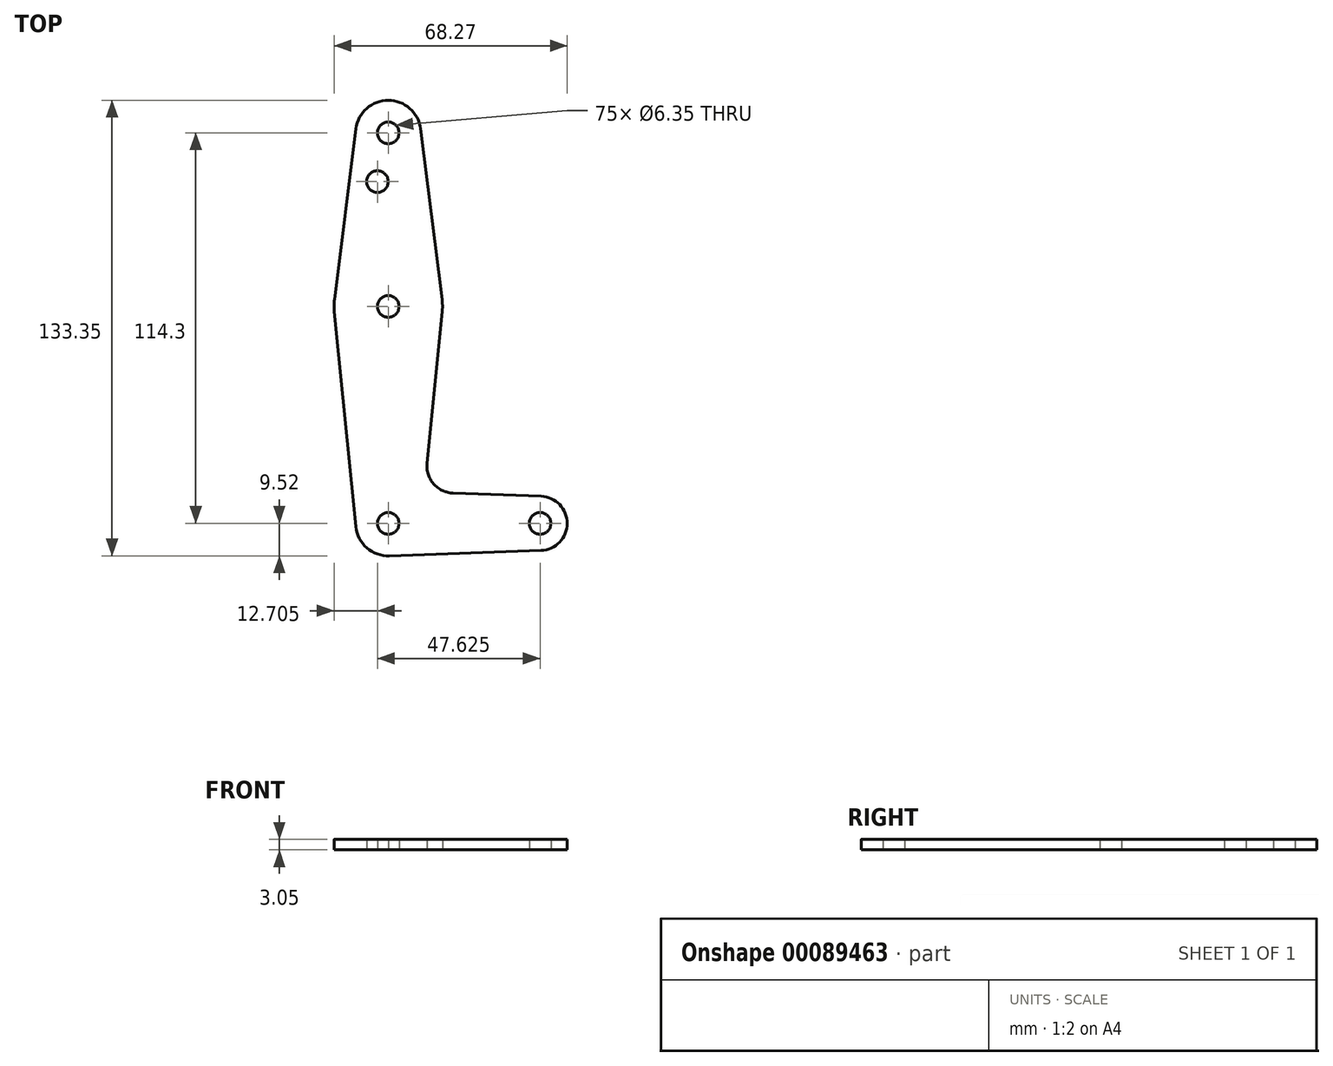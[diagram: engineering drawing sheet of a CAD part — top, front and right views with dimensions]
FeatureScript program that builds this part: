
annotation { "Feature Type Name" : "Feature", "Feature Type Description" : "" }
export const myFeature = defineFeature(function(context is Context, id is Id, definition is map)
    precondition{}
    {
        {
            var Q0;
            Q0=qCreatedBy(makeId("Top.planeOp"),FACE);
            var sketch = newSketch(context, id + "F0", { "sketchPlane" : qUnion([Q0])});
            skLineSegment(sketch, "E0", {"start": v(0, 0) * mm, "end": v(0, 114.3) * mm, "construction": true});
            skLineSegment(sketch, "E1", {"start": v(0, 0) * mm, "end": v(44.45, 0) * mm, "construction": true});
            skCircle(sketch, "E2", {"center": v(0, 0) * mm, "radius": 9.53 * mm});
            skCircle(sketch, "E3", {"center": v(0, 63.5) * mm, "radius": 15.88 * mm});
            skCircle(sketch, "E4", {"center": v(0, 114.3) * mm, "radius": 9.53 * mm});
            skCircle(sketch, "E5", {"center": v(44.45, 0) * mm, "radius": 7.94 * mm});
            skLineSegment(sketch, "E6", {"start": v(-9.45, 115.5) * mm, "end": v(-15.75, 65.48) * mm});
            skLineSegment(sketch, "E7", {"start": v(-15.8, 61.91) * mm, "end": v(-9.48, -0.95) * mm});
            skLineSegment(sketch, "E8", {"start": v(9.45, 115.5) * mm, "end": v(15.75, 65.48) * mm});
            skLineSegment(sketch, "E9", {"start": v(15.8, 61.91) * mm, "end": v(11.34, 17.6) * mm});
            skLineSegment(sketch, "E10", {"start": v(18.97, 8.85) * mm, "end": v(44.73, 7.93) * mm});
            skLineSegment(sketch, "E11", {"start": v(0.34, -9.52) * mm, "end": v(44.73, -7.93) * mm});
            skCircle(sketch, "E12", {"center": v(-3.17, 100.03) * mm, "radius": 3.18 * mm});
            skCircle(sketch, "E13", {"center": v(0, 63.5) * mm, "radius": 3.18 * mm});
            skCircle(sketch, "E14", {"center": v(0, 0) * mm, "radius": 3.18 * mm});
            skCircle(sketch, "E15", {"center": v(44.45, 0) * mm, "radius": 3.18 * mm});
            skCircle(sketch, "E16", {"center": v(0, 114.3) * mm, "radius": 3.18 * mm});
            skArc(sketch, "E17.filletArc", {"start": v(11.34, 17.6) * mm, "mid": v(13.26, 11.57) * mm, "end": v(18.97, 8.85) * mm});
            skSolve(sketch);
        }
        {
            var Q0;
            Q0 = qSketchRegion(id + "F0", true);
            extrude(context, id + "F1", {"entities" : qUnion([Q0]), "depth" : 3.05 * mm});
        }
    });
